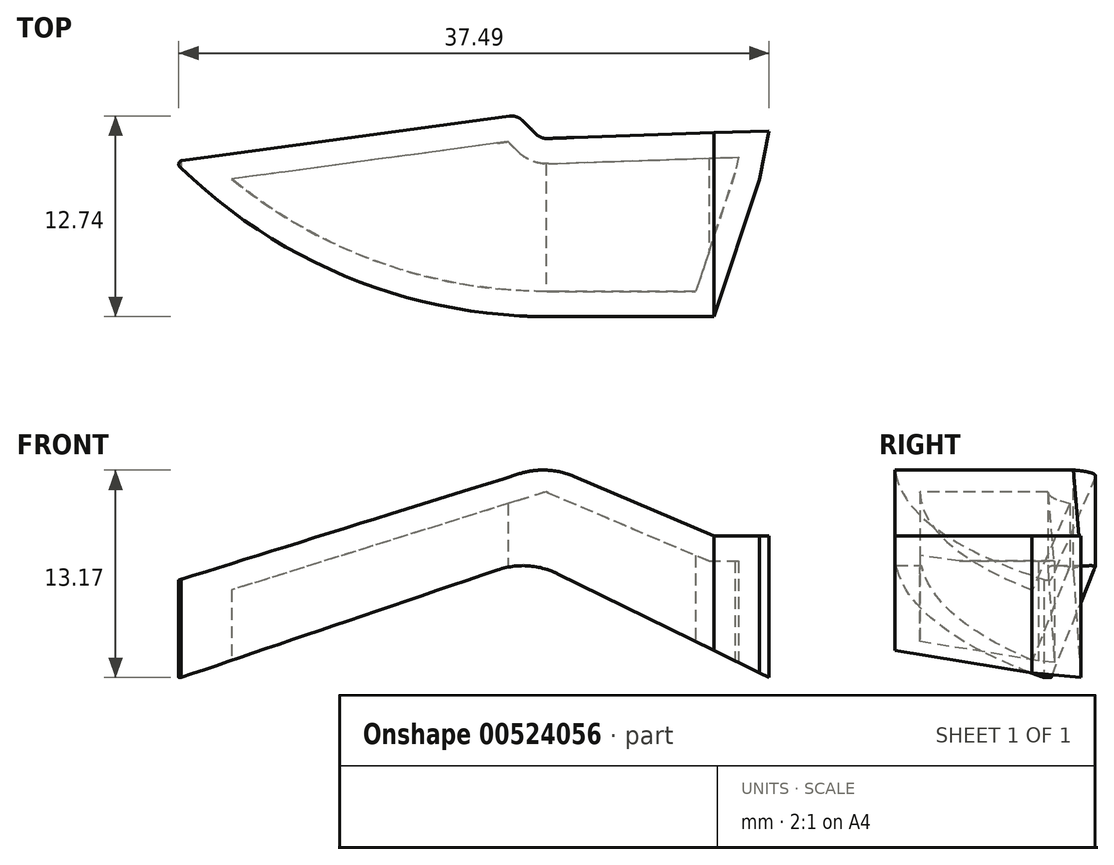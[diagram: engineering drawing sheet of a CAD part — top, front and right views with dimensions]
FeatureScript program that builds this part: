
annotation { "Feature Type Name" : "Feature", "Feature Type Description" : "" }
export const myFeature = defineFeature(function(context is Context, id is Id, definition is map)
    precondition{}
    {
        {
            var Q0;
            Q0=qCreatedBy(makeId("Top.planeOp"),FACE);
            var sketch = newSketch(context, id + "F0", { "sketchPlane" : qUnion([Q0])});
            skLineSegment(sketch, "E0", {"start": v(0, 0) * mm, "end": v(-0.6, -3.1) * mm});
            skLineSegment(sketch, "E1", {"start": v(-0.6, -3.1) * mm, "end": v(-3.5, -11.8) * mm});
            skLineSegment(sketch, "E2", {"start": v(-3.5, -11.8) * mm, "end": v(-14.1, -11.8) * mm});
            skLineSegment(sketch, "E3", {"start": v(-37.27, -1.87) * mm, "end": v(-16.5, 0.93) * mm});
            skLineSegment(sketch, "E4", {"start": v(-15.65, 0.65) * mm, "end": v(-14.8, -0.2) * mm});
            skLineSegment(sketch, "E5", {"start": v(-14.07, -0.49) * mm, "end": v(0, 0) * mm});
            skPoint(sketch, "E6.visualSharp", {"position": v(-14.5, -0.5) * mm});
            skArc(sketch, "E6.filletArc", {"start": v(-14.8, -0.2) * mm, "mid": v(-14.47, -0.42) * mm, "end": v(-14.07, -0.49) * mm});
            skPoint(sketch, "E7.visualSharp", {"position": v(-16, 1) * mm});
            skArc(sketch, "E7.filletArc", {"start": v(-15.65, 0.65) * mm, "mid": v(-16.04, 0.9) * mm, "end": v(-16.5, 0.93) * mm});
            skPoint(sketch, "E8.visualSharp", {"position": v(-38.2, -2) * mm});
            skArc(sketch, "E8.filletArc", {"start": v(-37.27, -1.87) * mm, "mid": v(-37.48, -2.1) * mm, "end": v(-37.33, -2.35) * mm});
            skArc(sketch, "E9", {"start": v(-37.33, -2.35) * mm, "mid": v(-26.64, -9.35) * mm, "end": v(-14.1, -11.8) * mm});
            skSolve(sketch);
        }
        {
            var Q0;
            Q0 = qSketchRegion(id + "F0", true);
            extrude(context, id + "F1", {"entities" : qUnion([Q0]), "depth" : 13.5 * mm, "offsetDistance" : 25 * mm});
        }
        {
            var Q0;
            Q0=makeQuery(id+"F1.opExtrude","SWEPT_FACE",FACE,{"disambiguationData":[OSD([sQuery(id+"F0.wireOp",EDGE,"E2")])]});
            var sketch = newSketch(context, id + "F2", { "sketchPlane" : qUnion([Q0])});
            skLineSegment(sketch, "E10", {"start": v(-14.1, 13.5) * mm, "end": v(-3.5, 9) * mm});
            skLineSegment(sketch, "E11", {"start": v(-3.5, 9) * mm, "end": v(0, 9) * mm});
            skLineSegment(sketch, "E12", {"start": v(0, 9) * mm, "end": v(0, 13.5) * mm});
            skLineSegment(sketch, "E13", {"start": v(0, 13.5) * mm, "end": v(-14.1, 13.5) * mm});
            skSolve(sketch);
        }
        {
            var Q0;
            Q0 = qSketchRegion(id + "F2", true);
            var Q1;
            Q1=makeQuery(id+"F1.opExtrude","SWEPT_FACE",FACE,{"disambiguationData":[OSD([sQuery(id+"F0.wireOp",EDGE,"E5")])]});
            extrude(context, id + "F3", {"entities" : qUnion([Q0]), "operationType" : NewBodyOperationType.REMOVE, "endBound" : BoundingType.UP_TO_SURFACE, "oppositeDirection" : true, "depth" : 13.5 * mm, "endBoundEntityFace" : qUnion([Q1]), "offsetDistance" : 25 * mm});
        }
        {
            var Q0;
            Q0=makeQuery(id+"F1.opExtrude","SWEPT_FACE",FACE,{"disambiguationData":[OSD([sQuery(id+"F0.wireOp",EDGE,"E2")])]});
            var sketch = newSketch(context, id + "F4", { "sketchPlane" : qUnion([Q0])});
            skLineSegment(sketch, "E14", {"start": v(0, 0) * mm, "end": v(-15.28, 7.5) * mm});
            skLineSegment(sketch, "E15", {"start": v(-15.28, 7.5) * mm, "end": v(-37.33, 0) * mm});
            skLineSegment(sketch, "E16", {"start": v(-37.33, 0) * mm, "end": v(0, 0) * mm});
            skSolve(sketch);
        }
        {
            var Q0;
            Q0 = qSketchRegion(id + "F4", true);
            var Q1;
            Q1=makeQuery(id+"F1.opExtrude","SWEPT_FACE",FACE,{"disambiguationData":[OSD([sQuery(id+"F0.wireOp",EDGE,"E3")])]});
            extrude(context, id + "F5", {"entities" : qUnion([Q0]), "operationType" : NewBodyOperationType.REMOVE, "endBound" : BoundingType.UP_TO_SURFACE, "oppositeDirection" : true, "depth" : 25 * mm, "endBoundEntityFace" : qUnion([Q1]), "offsetDistance" : 25 * mm});
        }
        {
            var Q0;
            Q0=qCreatedBy(makeId("Front.planeOp"),FACE);
            var sketch = newSketch(context, id + "F6", { "sketchPlane" : qUnion([Q0])});
            skLineSegment(sketch, "E17", {"start": v(-14.07, 13.5) * mm, "end": v(-38.07, 6) * mm});
            skLineSegment(sketch, "E18", {"start": v(-38.07, 6) * mm, "end": v(-38.07, 13.5) * mm});
            skLineSegment(sketch, "E19", {"start": v(-38.07, 13.5) * mm, "end": v(-14.07, 13.5) * mm});
            skSolve(sketch);
        }
        {
            var Q0;
            Q0 = qSketchRegion(id + "F6", true);
            extrude(context, id + "F7", {"entities" : qUnion([Q0]), "operationType" : NewBodyOperationType.REMOVE, "depth" : 12 * mm, "offsetDistance" : 25 * mm});
        }
        {
            var Q0;
            Q0 = qSketchRegion(id + "F6", true);
            extrude(context, id + "F8", {"entities" : qUnion([Q0]), "operationType" : NewBodyOperationType.REMOVE, "oppositeDirection" : true, "depth" : 1 * mm, "offsetDistance" : 25 * mm});
        }
        {
            var Q0;
            Q0=makeQuery(id+"F5.boolean.opBoolean","COPY",FACE,{"derivedFrom":makeQuery(id+"F5.opExtrude","SWEPT_FACE",FACE,{"disambiguationData":[OSD([sQuery(id+"F4.wireOp",EDGE,"E15")])]})});
            var Q1;
            Q1=makeQuery(id+"F5.boolean.opBoolean","COPY",FACE,{"derivedFrom":makeQuery(id+"F5.opExtrude","SWEPT_FACE",FACE,{"disambiguationData":[OSD([sQuery(id+"F4.wireOp",EDGE,"E14")])]})});
            shell(context, id + "F9", {"entities" : qUnion([Q0, Q1]), "thickness" : 1.6 * mm});
        }
        {
            var Q0;
            Q0=makeQuery(id+"F7.boolean.opBoolean","INTERSECT",EDGE,{"derivedFrom":[makeQuery(id+"F3.boolean.opBoolean","COPY",FACE,{"derivedFrom":makeQuery(id+"F3.opExtrude","SWEPT_FACE",FACE,{"disambiguationData":[OSD([sQuery(id+"F2.wireOp",EDGE,"E10")])]})}),makeQuery(id+"F7.opExtrude","SWEPT_FACE",FACE,{"disambiguationData":[OSD([sQuery(id+"F6.wireOp",EDGE,"E17")])]})]});
            var Q1;
            Q1=makeQuery(id+"F9.opShell","OFFSET_EDGE",EDGE,{"disambiguationData":[OSD([sQuery(id+"F4.wireOp",EDGE,"E14"),sQuery(id+"F4.wireOp",EDGE,"E15")])]});
            var Q2;
            Q2=makeQuery(id+"F5.boolean.opBoolean","COPY",EDGE,{"derivedFrom":makeQuery(id+"F5.opExtrude","SWEPT_EDGE",EDGE,{"disambiguationData":[OSD([sQuery(id+"F4.wireOp",EDGE,"E14"),sQuery(id+"F4.wireOp",EDGE,"E15")])]})});
            fillet(context, id + "F10", {"entities" : qUnion([Q0, Q1, Q2]), "radius" : 5 * mm, "tangentPropagation" : true, "allowEdgeOverflow" : false});
        }
    });
